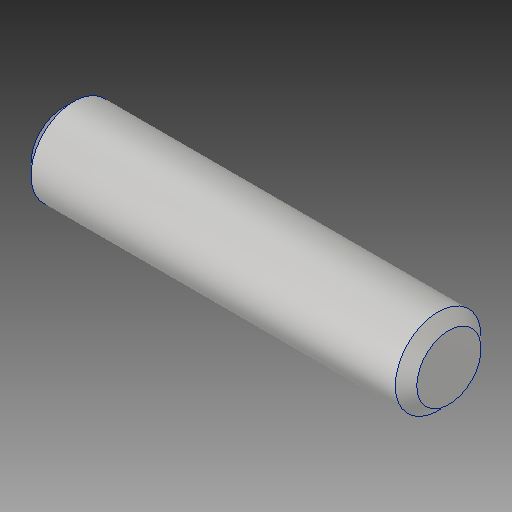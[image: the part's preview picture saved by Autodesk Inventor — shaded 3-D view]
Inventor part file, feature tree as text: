
AUTODESK INVENTOR PART (.ipt)
format: ipt  version: 2017 (Build 210142000, 142)  size: 93,184 bytes
history: native  units: in
note: dims shown in document units (in); Inventor stores cm internally (conversion verified against a paired STEP export)
features: chamfer x1
ambient origin geometry x8: Origin, YZ Plane, XZ Plane, XY Plane, X Axis, Y Axis, Z Axis, Center Point
bodies: Solid1 (feature_tree)
feature tree (1):
  chamfer  "Chamfer1"  [1 undecoded]
note: 1 required parameter value undecoded (feature->parameter linkage not recoverable at this tier; creation-order binding heuristic only, values carry confidence <= 0.55)
